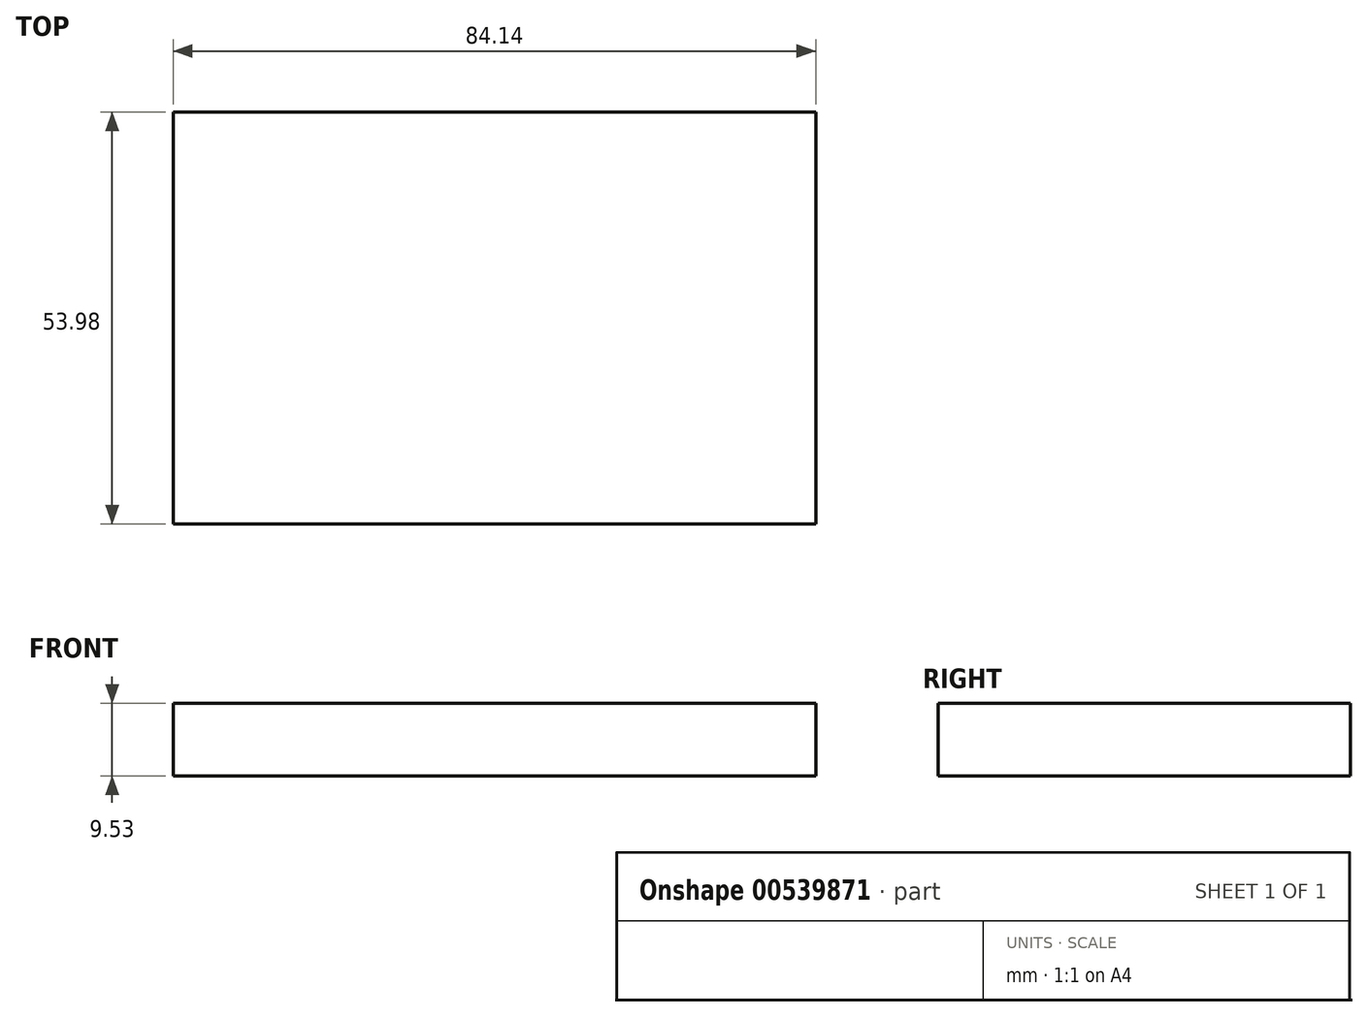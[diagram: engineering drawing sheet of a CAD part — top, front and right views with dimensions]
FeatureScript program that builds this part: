
annotation { "Feature Type Name" : "Feature", "Feature Type Description" : "" }
export const myFeature = defineFeature(function(context is Context, id is Id, definition is map)
    precondition{}
    {
        {
            var Q0;
            Q0=qCreatedBy(makeId("Top.planeOp"),FACE);
            var sketch = newSketch(context, id + "F0", { "sketchPlane" : qUnion([Q0])});
            skLineSegment(sketch, "E0.bottom", {"start": v(-42.07, 26.99) * mm, "end": v(42.07, 26.99) * mm});
            skLineSegment(sketch, "E0.top", {"start": v(-42.07, -26.99) * mm, "end": v(42.07, -26.99) * mm});
            skLineSegment(sketch, "E0.left", {"start": v(-42.07, 26.99) * mm, "end": v(-42.07, -26.99) * mm});
            skLineSegment(sketch, "E0.right", {"start": v(42.07, 26.99) * mm, "end": v(42.07, -26.99) * mm});
            skPoint(sketch, "E0.middle", {"position": v(0, 0) * mm});
            skSolve(sketch);
        }
        {
            var Q0;
            Q0 = qSketchRegion(id + "F0", true);
            extrude(context, id + "F1", {"entities" : qUnion([Q0]), "depth" : 9.52 * mm, "offsetDistance" : 25.4 * mm});
        }
    });
